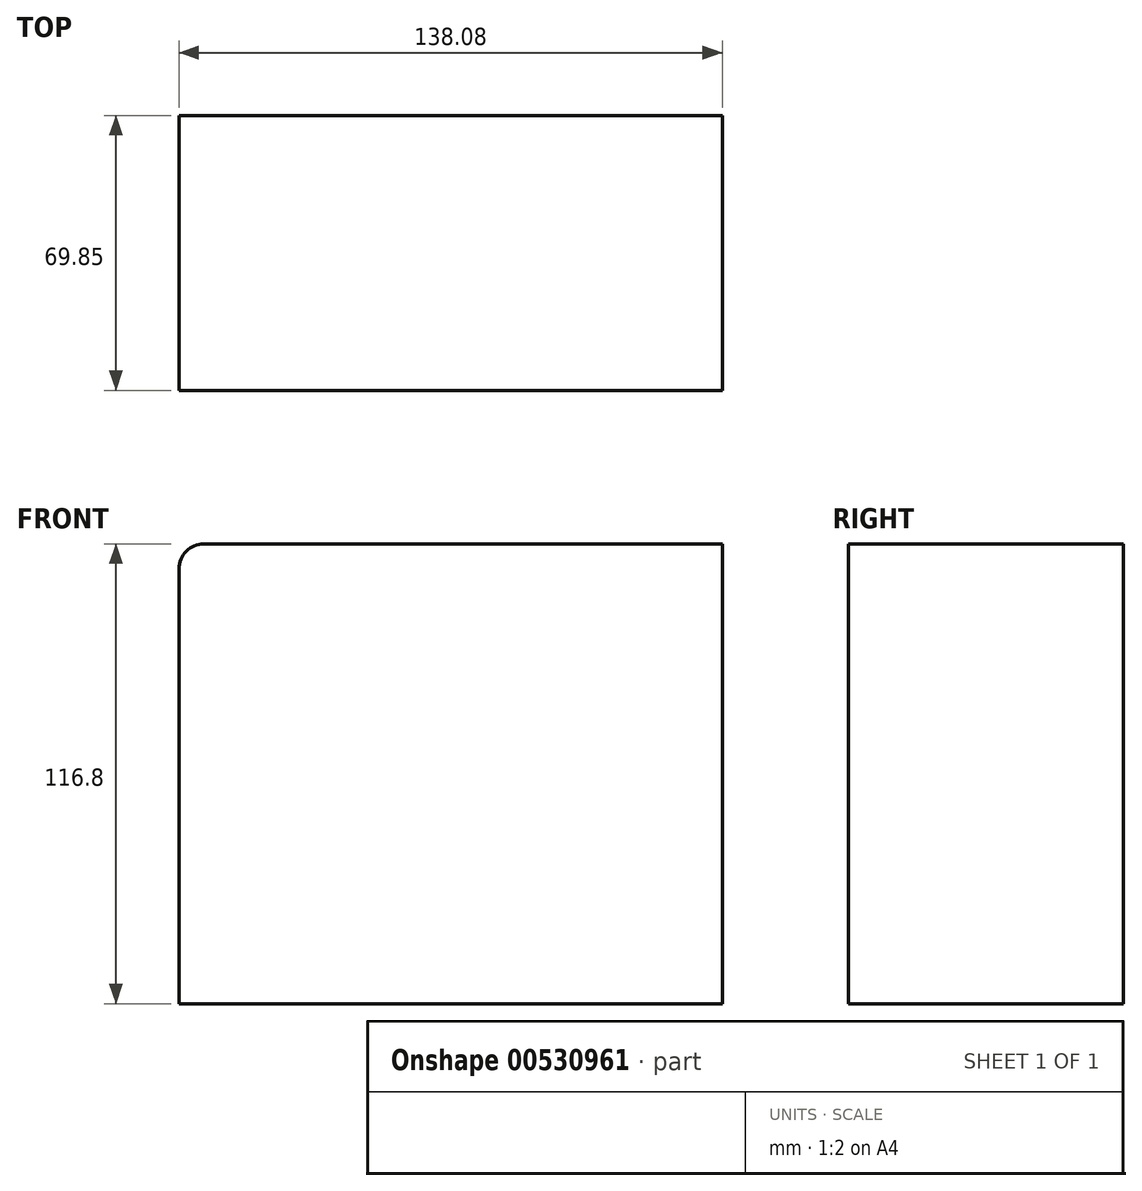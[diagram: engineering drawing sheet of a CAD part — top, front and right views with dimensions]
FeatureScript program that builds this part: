
annotation { "Feature Type Name" : "Feature", "Feature Type Description" : "" }
export const myFeature = defineFeature(function(context is Context, id is Id, definition is map)
    precondition{}
    {
        {
            var Q0;
            Q0=qCreatedBy(makeId("Front.planeOp"),FACE);
            var sketch = newSketch(context, id + "F0", { "sketchPlane" : qUnion([Q0])});
            skLineSegment(sketch, "E0.bottom", {"start": v(-62.71, 56.7) * mm, "end": v(69.02, 56.7) * mm});
            skLineSegment(sketch, "E0.top", {"start": v(-69.06, -60.1) * mm, "end": v(69.02, -60.1) * mm});
            skLineSegment(sketch, "E0.left", {"start": v(-69.06, 50.36) * mm, "end": v(-69.06, -60.1) * mm});
            skLineSegment(sketch, "E0.right", {"start": v(69.02, 56.7) * mm, "end": v(69.02, -60.1) * mm});
            skPoint(sketch, "E1.visualSharp", {"position": v(-69.06, 56.7) * mm});
            skArc(sketch, "E1.filletArc", {"start": v(-62.71, 56.7) * mm, "mid": v(-67.2, 54.85) * mm, "end": v(-69.06, 50.36) * mm});
            skSolve(sketch);
        }
        {
            var Q0;
            Q0 = qSketchRegion(id + "F0", true);
            extrude(context, id + "F1", {"entities" : qUnion([Q0]), "depth" : 69.85 * mm, "offsetDistance" : 25.4 * mm});
        }
    });
